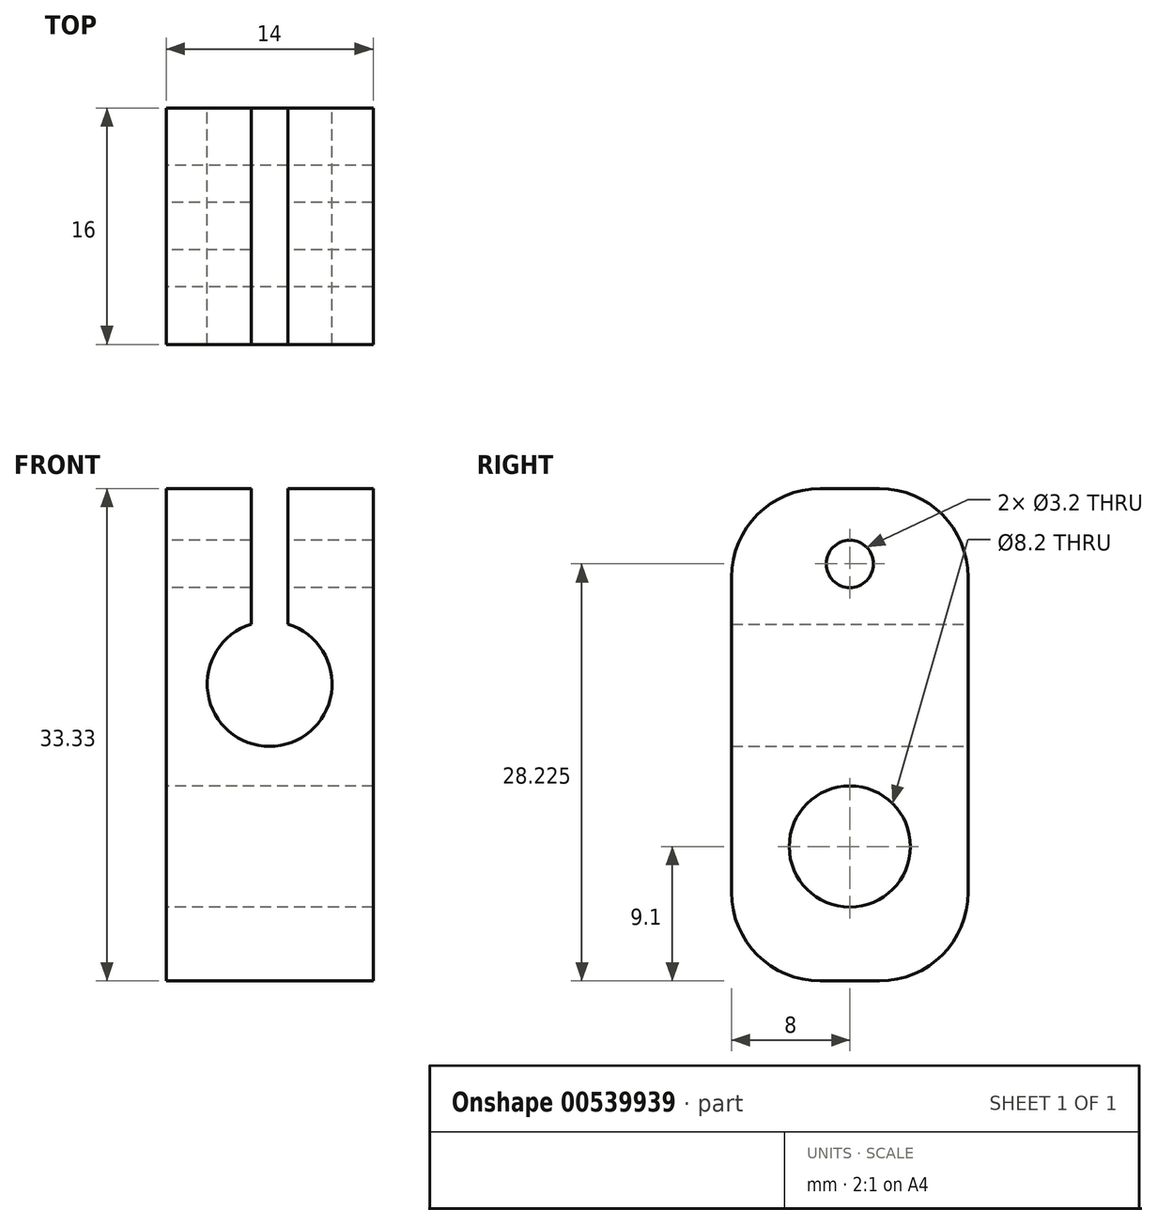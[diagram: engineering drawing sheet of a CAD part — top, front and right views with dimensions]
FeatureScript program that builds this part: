
annotation { "Feature Type Name" : "Feature", "Feature Type Description" : "" }
export const myFeature = defineFeature(function(context is Context, id is Id, definition is map)
    precondition{}
    {
        {
            var Q0;
            Q0=qCreatedBy(makeId("Right.planeOp"),FACE);
            var sketch = newSketch(context, id + "F0", { "sketchPlane" : qUnion([Q0])});
            skLineSegment(sketch, "E0.bottom", {"start": v(0, 0) * mm, "end": v(16, 0) * mm});
            skLineSegment(sketch, "E0.top", {"start": v(0, 33.33) * mm, "end": v(16, 33.33) * mm});
            skLineSegment(sketch, "E0.left", {"start": v(0, 0) * mm, "end": v(0, 33.33) * mm});
            skLineSegment(sketch, "E0.right", {"start": v(16, 0) * mm, "end": v(16, 33.33) * mm});
            skCircle(sketch, "E1", {"center": v(8, 9.1) * mm, "radius": 4.1 * mm});
            skCircle(sketch, "E2", {"center": v(8, 20.1) * mm, "radius": 4.22 * mm});
            skCircle(sketch, "E3", {"center": v(8, 28.23) * mm, "radius": 1.6 * mm});
            skSolve(sketch);
        }
        {
            var Q0;
            Q0 = qSketchRegion(id + "F0", true);
            var Q1;
            Q1=makeQuery(id+"F0.imprint","IMPRINT",FACE,{"disambiguationData":[TD([[makeQuery(id+"F0.imprint","IMPRINT",EDGE,{"derivedFrom":sQuery(id+"F0.wireOp",EDGE,"E2")}),1.0]])]});
            extrude(context, id + "F1", {"entities" : qUnion([Q0, Q1]), "depth" : 14 * mm, "offsetDistance" : 25 * mm});
        }
        {
            var Q0;
            Q0=makeQuery(id+"F1.opExtrude","SWEPT_FACE",FACE,{"disambiguationData":[OSD([sQuery(id+"F0.wireOp",EDGE,"E0.right")])]});
            var sketch = newSketch(context, id + "F2", { "sketchPlane" : qUnion([Q0])});
            skCircle(sketch, "E4", {"center": v(-7, 20.1) * mm, "radius": 4.22 * mm});
            skLineSegment(sketch, "E5", {"start": v(-8.25, 33.33) * mm, "end": v(-8.25, 24.14) * mm});
            skLineSegment(sketch, "E6", {"start": v(-5.75, 33.33) * mm, "end": v(-5.75, 24.14) * mm});
            skSolve(sketch);
        }
        {
            var Q0;
            Q0 = qSketchRegion(id + "F2", true);
            var Q1;
            {var subQ0=sQuery(id+"F2.wireOp",EDGE,"E5");Q1=makeQuery(id+"F2.imprint","IMPRINT",FACE,{"disambiguationData":[TD([[makeQuery(id+"F2.imprint","IMPRINT",EDGE,{"derivedFrom":subQ0}),1.0]])]});}
            extrude(context, id + "F3", {"entities" : qUnion([Q0, Q1]), "operationType" : NewBodyOperationType.REMOVE, "endBound" : BoundingType.UP_TO_NEXT, "oppositeDirection" : true, "depth" : 25 * mm, "offsetDistance" : 25 * mm});
        }
        {
            var Q0;
            Q0=makeQuery(id+"F1.opExtrude","SWEPT_EDGE",EDGE,{"disambiguationData":[OSD([sQuery(id+"F0.wireOp",EDGE,"E0.bottom"),sQuery(id+"F0.wireOp",EDGE,"E0.right")])]});
            var Q1;
            Q1=makeQuery(id+"F1.opExtrude","SWEPT_EDGE",EDGE,{"disambiguationData":[OSD([sQuery(id+"F0.wireOp",EDGE,"E0.bottom"),sQuery(id+"F0.wireOp",EDGE,"E0.left")])]});
            var Q2;
            {var subQ0=sQuery(id+"F0.wireOp",EDGE,"E0.left");var subQ1=sQuery(id+"F0.wireOp",EDGE,"E0.top");Q2=makeQuery(id+"F3.boolean.opBoolean","SPLIT",EDGE,{"disambiguationData":[TD([makeQuery(id+"F3.opExtrude","SWEPT_FACE",FACE,{"disambiguationData":[OSD([sQuery(id+"F2.wireOp",EDGE,"E5")])]})])],"derivedFrom":makeQuery(id+"F1.opExtrude","SWEPT_EDGE",EDGE,{"disambiguationData":[OSD([subQ1,subQ0])]})});}
            var Q3;
            {var subQ0=sQuery(id+"F0.wireOp",EDGE,"E0.left");var subQ1=sQuery(id+"F0.wireOp",EDGE,"E0.top");Q3=makeQuery(id+"F3.boolean.opBoolean","SPLIT",EDGE,{"disambiguationData":[TD([makeQuery(id+"F3.opExtrude","SWEPT_FACE",FACE,{"disambiguationData":[OSD([sQuery(id+"F2.wireOp",EDGE,"E6")])]})])],"derivedFrom":makeQuery(id+"F1.opExtrude","SWEPT_EDGE",EDGE,{"disambiguationData":[OSD([subQ1,subQ0])]})});}
            var Q4;
            {var subQ0=sQuery(id+"F0.wireOp",EDGE,"E0.right");var subQ1=sQuery(id+"F0.wireOp",EDGE,"E0.top");Q4=makeQuery(id+"F3.boolean.opBoolean","SPLIT",EDGE,{"disambiguationData":[TD([makeQuery(id+"F3.opExtrude","SWEPT_FACE",FACE,{"disambiguationData":[OSD([sQuery(id+"F2.wireOp",EDGE,"E5")])]})])],"derivedFrom":makeQuery(id+"F1.opExtrude","SWEPT_EDGE",EDGE,{"disambiguationData":[OSD([subQ1,subQ0])]})});}
            var Q5;
            {var subQ0=sQuery(id+"F0.wireOp",EDGE,"E0.right");var subQ1=sQuery(id+"F0.wireOp",EDGE,"E0.top");Q5=makeQuery(id+"F3.boolean.opBoolean","SPLIT",EDGE,{"disambiguationData":[TD([makeQuery(id+"F3.opExtrude","SWEPT_FACE",FACE,{"disambiguationData":[OSD([sQuery(id+"F2.wireOp",EDGE,"E6")])]})])],"derivedFrom":makeQuery(id+"F1.opExtrude","SWEPT_EDGE",EDGE,{"disambiguationData":[OSD([subQ1,subQ0])]})});}
            fillet(context, id + "F4", {"entities" : qUnion([Q0, Q1, Q2, Q3, Q4, Q5]), "radius" : 6 * mm, "tangentPropagation" : true, "allowEdgeOverflow" : false});
        }
    });
